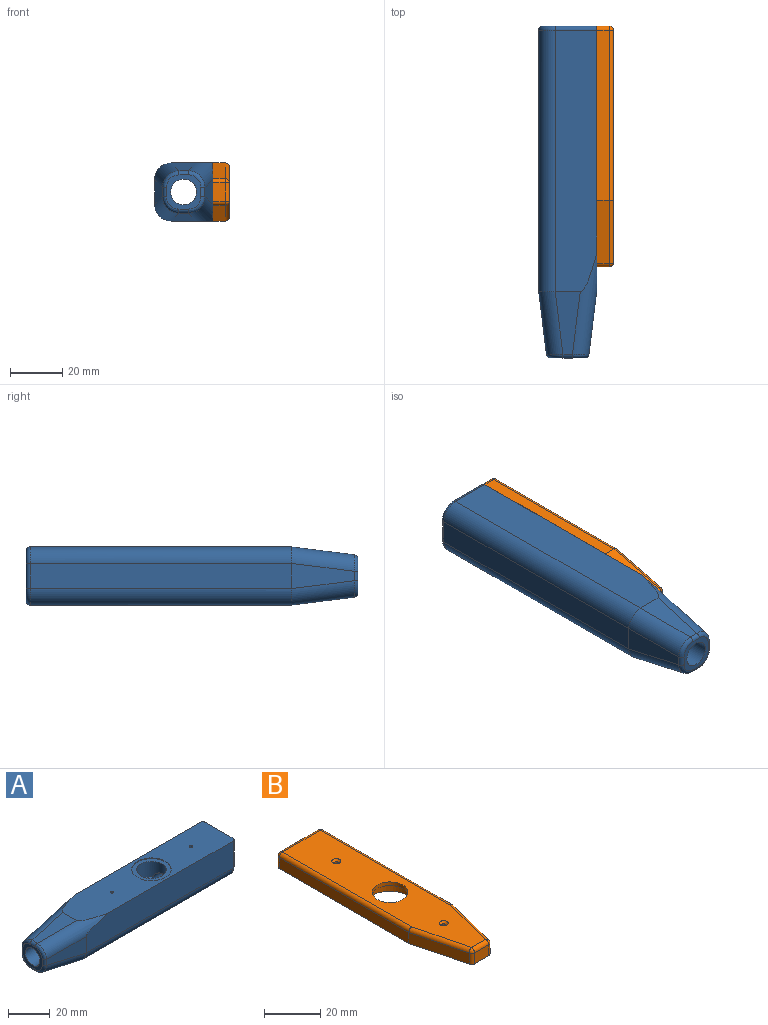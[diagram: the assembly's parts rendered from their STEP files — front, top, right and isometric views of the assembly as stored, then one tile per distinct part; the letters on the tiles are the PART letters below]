
ASSEMBLY  parts=2 mates=1
PART A: 39 faces, bbox 127x26x24.6 mm
  f0: cone r=0mm half-angle=59deg, axis (0,0,1), area 18.9mm2, adj f17,f25
  f1: plane 100.01x15.88mm, normal (0,-1,0), area 1553.8mm2, adj f5,f8,f11,f15,f34
  f2: plane 20.64x19.05mm, normal (1,0,0), area 305.9mm2, adj f5,f25,f34,f35,f36,f37,f38
  f3: plane 100.01x15.88mm, normal (0,1,0), area 1553.8mm2, adj f5,f9,f13,f16,f38
  f4: plane 13.07x13.07mm, normal (-1,0,0), area 74.3mm2, adj f25,f26,f27,f28,f29,f30,f31,f32
  f5: plane 101.6x22.23mm, normal (0,0,1), area 1900.2mm2, adj f1,f2,f3,f10,f15,f16,f19,f22
  f6: plane 100.01x9.53mm, normal (0,0,-1), area 952.6mm2, adj f7,f11,f13,f36
  f7: plane 24.01x9.62mm, normal (-0.12,0,-0.99), area 160.2mm2, adj f6,f11,f12,f13,f14,f31
  f8: plane 24.01x9.62mm, normal (-0.12,-0.99,0), area 160.2mm2, adj f1,f11,f12,f15,f32
  f9: plane 24.01x9.62mm, normal (-0.12,0.99,0), area 160.2mm2, adj f3,f13,f14,f16,f27
  f10: plane 24.01x9.62mm, normal (-0.12,0,0.99), area 160.2mm2, adj f5,f15,f16,f28
  f11: cylinder r=6.35mm len=100.17mm, axis (1,0,0), area 998.6mm2, adj f1,f6,f7,f8,f12,f35
  f12: cylinder r=6.35mm len=24.33mm, axis (-0.98,0.12,0.12), area 239.2mm2, adj f7,f8,f11,f33
  f13: cylinder r=6.35mm len=100.17mm, axis (-1,0,0), area 998.6mm2, adj f3,f6,f7,f9,f14,f37
  f14: cylinder r=6.35mm len=24.33mm, axis (-0.98,-0.12,0.12), area 239.2mm2, adj f7,f9,f13,f29
  f15: cylinder r=6.35mm len=39.36mm, axis (0.98,-0.12,0.12), area 291.6mm2, adj f1,f5,f8,f10,f30
  f16: cylinder r=6.35mm len=39.36mm, axis (0.98,0.12,0.12), area 291.6mm2, adj f3,f5,f9,f10,f26
  f17: cylinder r=7.14mm len=14.29mm, axis (0,0,1), area 360.4mm2, adj f0,f18,f20,f25
  f18: plane 19.05x19.05mm, normal (0,0,1), area 124.7mm2, adj f17,f19
  f19: cylinder r=9.53mm len=19.05mm, axis (0,0,1), area 23.9mm2, adj f5,f18
  f20: cone r=0mm half-angle=59deg, axis (0,0,1), area 18.9mm2, adj f17,f25
  f21: cone r=0mm half-angle=59deg, axis (0,0,1), area 2.3mm2, adj f22
  f22: cylinder r=0.79mm len=4.76mm, axis (0,0,1), area 23.8mm2, adj f5,f21
  f23: cone r=0mm half-angle=59deg, axis (0,0,1), area 2.3mm2, adj f24
  f24: cylinder r=0.79mm len=4.76mm, axis (0,0,1), area 23.8mm2, adj f5,f23
  f25: cylinder r=4.97mm len=127mm, axis (-1,0,0), area 3784.9mm2, adj f0,f2,f4,f17,f20
  f26: bspline ~6.3x6.3mm, area 20mm2, adj f4,f16,f27,f28
  f27: cylinder r=1.59mm len=3.62mm, axis (0,0,-1), area 8.3mm2, adj f4,f9,f26,f29
  f28: cylinder r=1.59mm len=3.62mm, axis (0,-1,0), area 8.3mm2, adj f4,f10,f26,f30
  f29: bspline ~6.63x6.63mm, area 20mm2, adj f4,f14,f27,f31
  f30: bspline ~6.3x6.3mm, area 20mm2, adj f4,f15,f28,f32
  f31: cylinder r=1.59mm len=3.62mm, axis (0,-1,0), area 8.3mm2, adj f4,f7,f29,f33
  f32: cylinder r=1.59mm len=3.62mm, axis (0,0,-1), area 8.3mm2, adj f4,f8,f30,f33
  f33: bspline ~6.63x6.63mm, area 20mm2, adj f4,f12,f31,f32
  f34: cylinder r=1.59mm len=15.88mm, axis (0,0,1), area 39.6mm2, adj f1,f2,f5,f35
  f35: torus R=4.76mm, axis (-1,0,0), area 22.6mm2, adj f2,f11,f34,f36
  f36: cylinder r=1.59mm len=9.53mm, axis (0,1,0), area 23.8mm2, adj f2,f6,f35,f37
  f37: torus R=4.76mm, axis (-1,0,0), area 22.6mm2, adj f2,f13,f36,f38
  f38: cylinder r=1.59mm len=15.88mm, axis (0,0,-1), area 39.6mm2, adj f2,f3,f5,f37
PART B: 29 faces, bbox 22.2x92.1x6.4 mm
  f0: cylinder r=6.35mm len=12.7mm, axis (0,0,1), area 63.3mm2, adj f5,f14
  f1: plane 19.05x4.76mm, normal (0,1,0), area 90.7mm2, adj f6,f15,f20,f21
  f2: plane 65.09x4.76mm, normal (-1,0,0), area 310mm2, adj f6,f7,f20,f26
  f3: plane 7.08x4.76mm, normal (0,-1,0), area 33.7mm2, adj f6,f19,f24,f25
  f4: plane 65.09x4.76mm, normal (1,0,0), area 310mm2, adj f6,f8,f15,f16
  f5: plane 88.9x19.05mm, normal (0,0,1), area 1407.3mm2, adj f0,f10,f12,f16,f18,f21,f24,f26
  f6: plane 92.08x22.23mm, normal (0,0,-1), area 1594.9mm2, adj f1,f2,f3,f4,f7,f8,f9,f11
  f7: plane 24.2x6.03mm, normal (-0.97,-0.24,0), area 118.8mm2, adj f2,f6,f25,f28
  f8: plane 24.2x6.03mm, normal (0.97,-0.24,0), area 118.8mm2, adj f4,f6,f18,f19
  f9: cylinder r=0.79mm len=5.56mm, axis (0,0,1), area 27.7mm2, adj f6,f10
  f10: cone r=0.79mm half-angle=45deg, axis (0,0,1), area 8.4mm2, adj f5,f9
  f11: cylinder r=0.79mm len=5.56mm, axis (0,0,1), area 27.7mm2, adj f6,f12
  f12: cone r=0.79mm half-angle=45deg, axis (0,0,1), area 8.4mm2, adj f5,f11
  f13: cylinder r=9.53mm len=19.05mm, axis (0,0,-1), area 285mm2, adj f6,f14
  f14: plane 19.05x19.05mm, normal (0,0,-1), area 158.3mm2, adj f0,f13
  f15: cylinder r=1.59mm len=4.76mm, axis (0,0,-1), area 11.9mm2, adj f1,f4,f6,f17
  f16: cylinder r=1.59mm len=65.09mm, axis (0,-1,0), area 162.1mm2, adj f4,f5,f17,f18
  f17: sphere r=1.59mm, area 4mm2, adj f15,f16,f21
  f18: cylinder r=1.59mm len=24.58mm, axis (0.24,0.97,0), area 62mm2, adj f5,f8,f16,f22
  f19: cylinder r=1.59mm len=4.76mm, axis (0,0,-1), area 10mm2, adj f3,f6,f8,f22
  f20: cylinder r=1.59mm len=4.76mm, axis (0,0,1), area 11.9mm2, adj f1,f2,f6,f23
  f21: cylinder r=1.59mm len=19.05mm, axis (1,0,0), area 47.5mm2, adj f1,f5,f17,f23
  f22: sphere r=1.59mm, area 3.3mm2, adj f18,f19,f24
  f23: sphere r=1.59mm, area 4mm2, adj f20,f21,f26
  f24: cylinder r=1.59mm len=7.08mm, axis (-1,0,0), area 17.7mm2, adj f3,f5,f22,f27
  f25: cylinder r=1.59mm len=4.76mm, axis (0,0,-1), area 10mm2, adj f3,f6,f7,f27
  f26: cylinder r=1.59mm len=65.09mm, axis (0,1,0), area 162.1mm2, adj f2,f5,f23,f28
  f27: sphere r=1.59mm, area 3.3mm2, adj f24,f25,f28
  f28: cylinder r=1.59mm len=24.58mm, axis (-0.24,0.97,0), area 62mm2, adj f5,f7,f26,f27
PLACE A rot(axis=(0.58,0.58,0.58),120deg) t=(-23.9,-10.41,20.85)mm
PLACE B rot(axis=(0,1,0),90deg) t=(-12.78,7.05,20.85)mm
MATE pin_slot B.f11 <-> A.f23  axis (-1,0,0) through (-12.78,-19.94,20.85)mm
